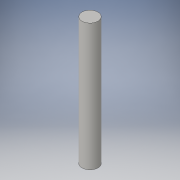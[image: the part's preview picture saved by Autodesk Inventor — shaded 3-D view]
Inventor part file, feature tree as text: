
AUTODESK INVENTOR PART (.ipt)
format: ipt  version: 2016 (Build 200138000, 138)  size: 84,992 bytes
history: native  units: in
note: dims shown in document units (in); Inventor stores cm internally (conversion verified against a paired STEP export)
features: extrude x1, sketch x1
ambient origin geometry x8: Origin, YZ Plane, XZ Plane, XY Plane, X Axis, Y Axis, Z Axis, Center Point
bodies: Solid1 (feature_tree)
feature tree (2):
  extrude  "Extrusion1"  Depth=3.0in TaperAngle=0.0deg
  sketch  "Sketch1"  dims[d0=0.375in d1=3.0in d2=0.0in]
